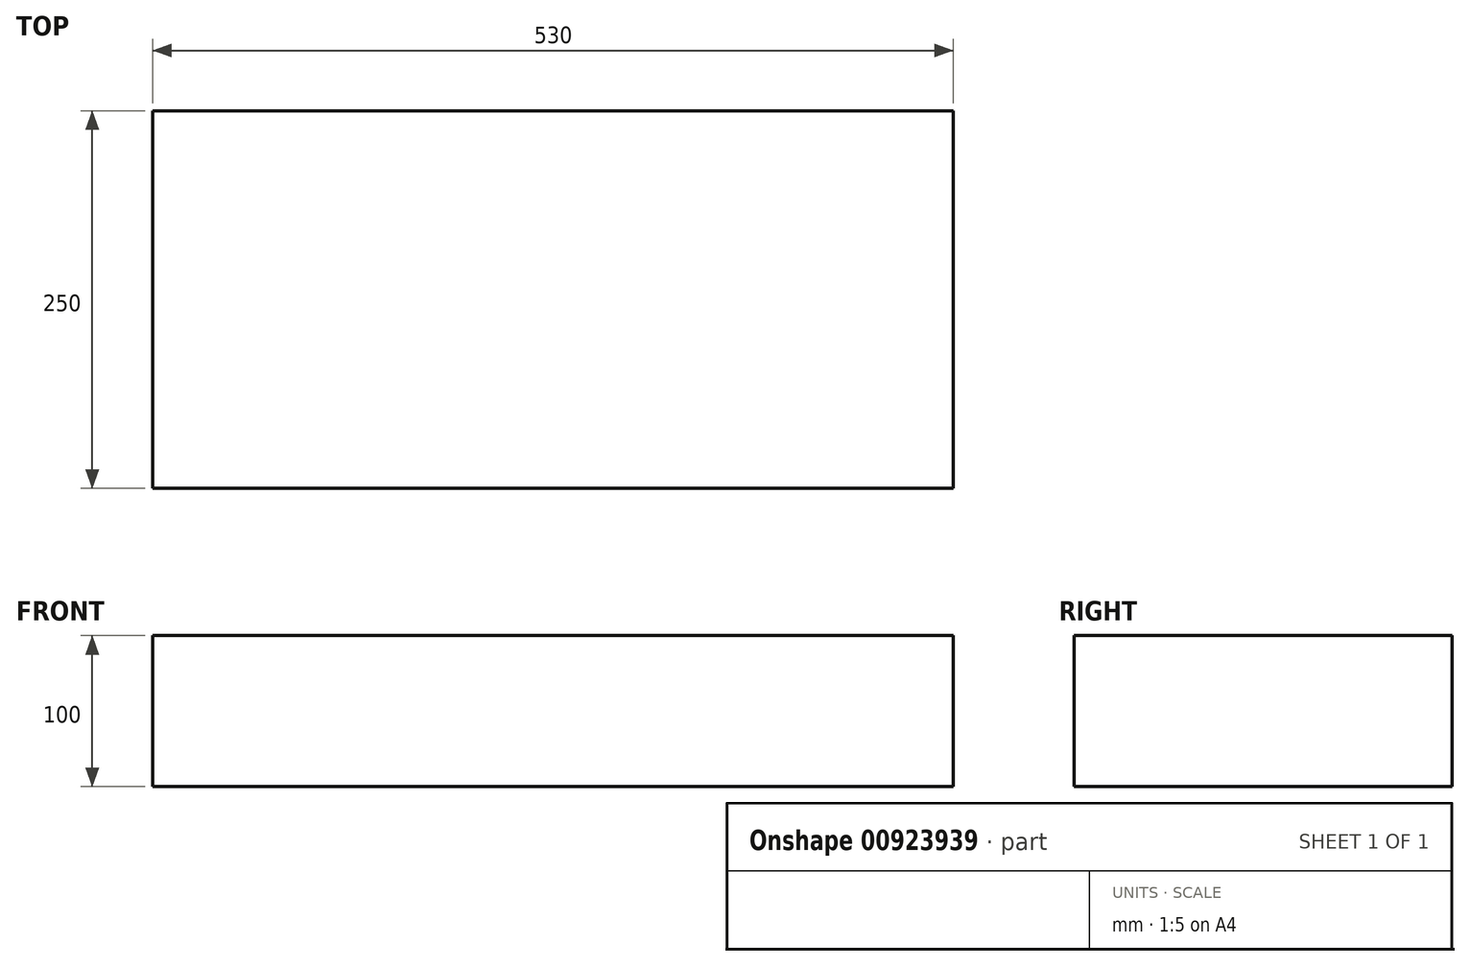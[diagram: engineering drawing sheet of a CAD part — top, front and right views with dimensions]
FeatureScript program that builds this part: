
annotation { "Feature Type Name" : "Feature", "Feature Type Description" : "" }
export const myFeature = defineFeature(function(context is Context, id is Id, definition is map)
    precondition{}
    {
        {
            var Q0;
            Q0=qCreatedBy(makeId("Top.planeOp"),FACE);
            var sketch = newSketch(context, id + "F0", { "sketchPlane" : qUnion([Q0])});
            skLineSegment(sketch, "E0.bottom", {"start": v(474.15, -37.5) * mm, "end": v(-55.85, -37.5) * mm});
            skLineSegment(sketch, "E0.top", {"start": v(474.15, 212.5) * mm, "end": v(-55.85, 212.5) * mm});
            skLineSegment(sketch, "E0.left", {"start": v(474.15, -37.5) * mm, "end": v(474.15, 212.5) * mm});
            skLineSegment(sketch, "E0.right", {"start": v(-55.85, -37.5) * mm, "end": v(-55.85, 212.5) * mm});
            skPoint(sketch, "E0.middle", {"position": v(209.15, 87.5) * mm});
            skSolve(sketch);
        }
        {
            var Q0;
            Q0=makeQuery(id+"F0.imprint","IMPRINT",FACE,{"disambiguationData":[TD([[makeQuery(id+"F0.imprint","IMPRINT",EDGE,{"derivedFrom":sQuery(id+"F0.wireOp",EDGE,"E0.bottom")}),-1.0]])]});
            extrude(context, id + "F1", {"entities" : qUnion([Q0]), "depth" : 100 * mm, "offsetDistance" : 25 * mm});
        }
    });
